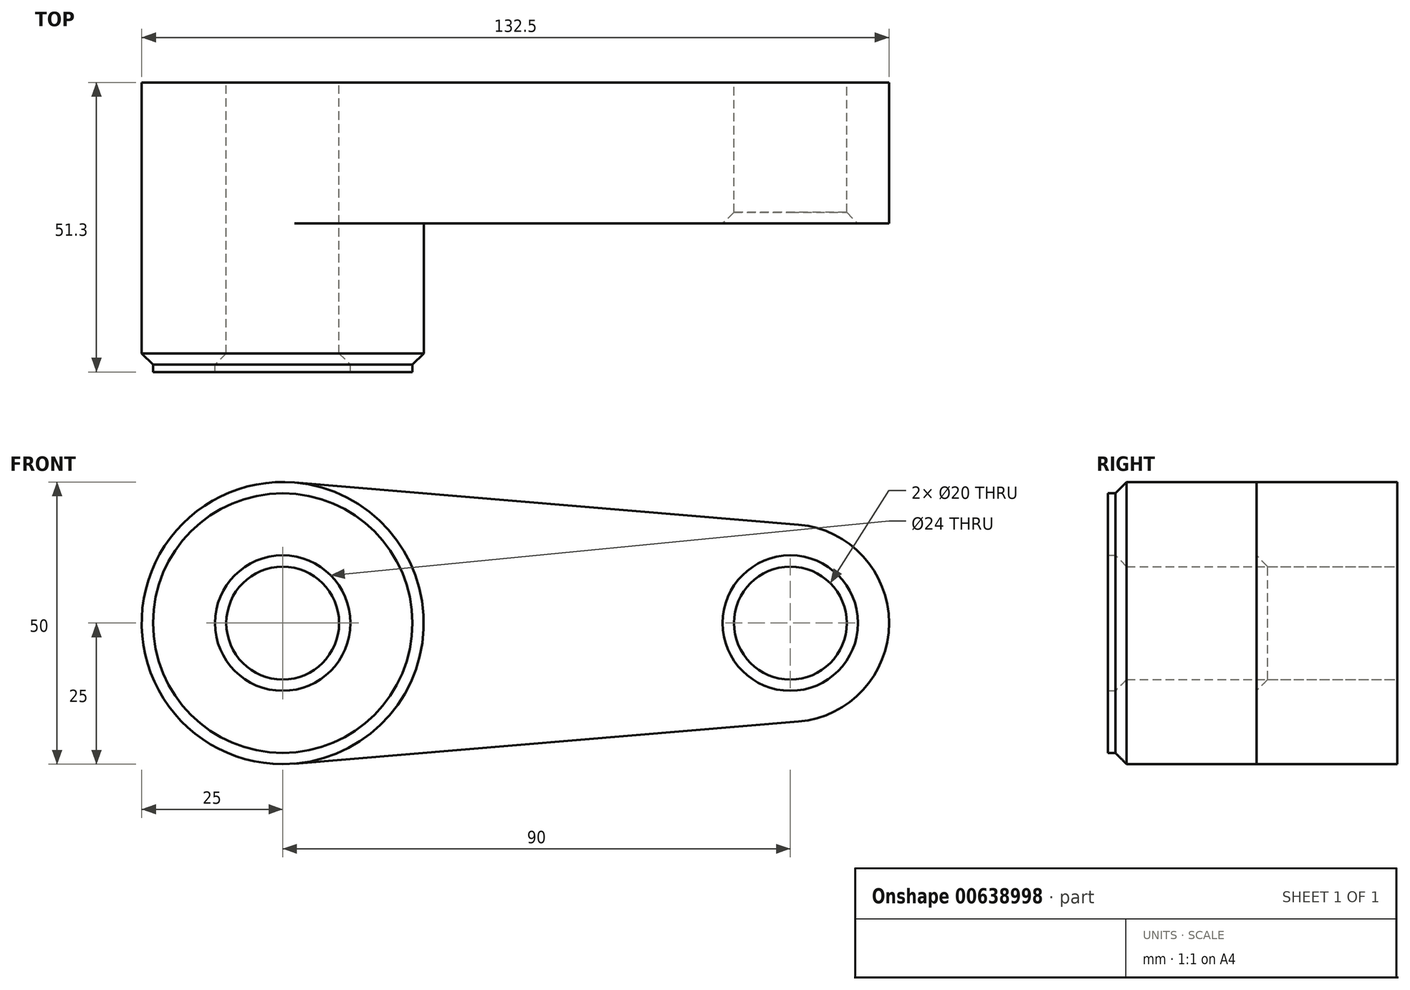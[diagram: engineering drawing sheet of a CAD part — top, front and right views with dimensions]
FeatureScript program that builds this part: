
annotation { "Feature Type Name" : "Feature", "Feature Type Description" : "" }
export const myFeature = defineFeature(function(context is Context, id is Id, definition is map)
    precondition{}
    {
        {
            var Q0;
            Q0=qCreatedBy(makeId("Front.planeOp"),FACE);
            var sketch = newSketch(context, id + "F0", { "sketchPlane" : qUnion([Q0])});
            skCircle(sketch, "E0", {"center": v(0, 0) * mm, "radius": 25 * mm});
            skCircle(sketch, "E1", {"center": v(90, 0) * mm, "radius": 17.5 * mm});
            skLineSegment(sketch, "E2", {"start": v(2.08, 24.91) * mm, "end": v(91.46, 17.44) * mm});
            skLineSegment(sketch, "E3", {"start": v(2.08, -24.91) * mm, "end": v(91.46, -17.44) * mm});
            skCircle(sketch, "E4", {"center": v(0, 0) * mm, "radius": 10 * mm});
            skCircle(sketch, "E5", {"center": v(90, 0) * mm, "radius": 10 * mm});
            skSolve(sketch);
        }
        {
            var Q0;
            Q0=qSketchRegion(id+"F0",true);
            extrude(context, id + "F1", {"entities" : qUnion([Q0]), "depth" : 25 * mm});
        }
        {
            var Q0;
            Q0=makeQuery(id+"F0.imprint","IMPRINT",FACE,{"disambiguationData":[TD([[makeQuery(id+"F0.imprint","IMPRINT",EDGE,{"derivedFrom":sQuery(id+"F0.wireOp",EDGE,"E4")}),-1.0]])]});
            extrude(context, id + "F2", {"entities" : qUnion([Q0]), "operationType" : NewBodyOperationType.ADD, "depth" : 50 * mm});
        }
        {
            var Q0;
            Q0=makeQuery(id+"F2.opExtrude","CAP_EDGE",EDGE,{"disambiguationData":[OSD([sQuery(id+"F0.wireOp",EDGE,"E0")])],"isStart":false});
            var Q1;
            Q1=makeQuery(id+"F2.opExtrude","CAP_EDGE",EDGE,{"disambiguationData":[OSD([sQuery(id+"F0.wireOp",EDGE,"E4")])],"isStart":false});
            var Q2;
            Q2=makeQuery(id+"F1.opExtrude","CAP_EDGE",EDGE,{"disambiguationData":[OSD([sQuery(id+"F0.wireOp",EDGE,"E5")])],"isStart":false});
            chamfer(context, id + "F3", {"entities" : qUnion([Q0, Q1, Q2]), "width" : 2 * mm, "tangentPropagation" : true});
        }
        {
            var Q0;
            Q0=makeQuery(id+"F2.opExtrude","CAP_FACE",FACE,{"disambiguationData":[OSD([sQuery(id+"F0.wireOp",EDGE,"E0"),sQuery(id+"F0.wireOp",EDGE,"E4")])],"isStart":false});
            extrude(context, id + "F4", {"entities" : qUnion([Q0]), "operationType" : NewBodyOperationType.ADD, "depth" : 1.3 * mm, "offsetDistance" : 25 * mm});
        }
    });
